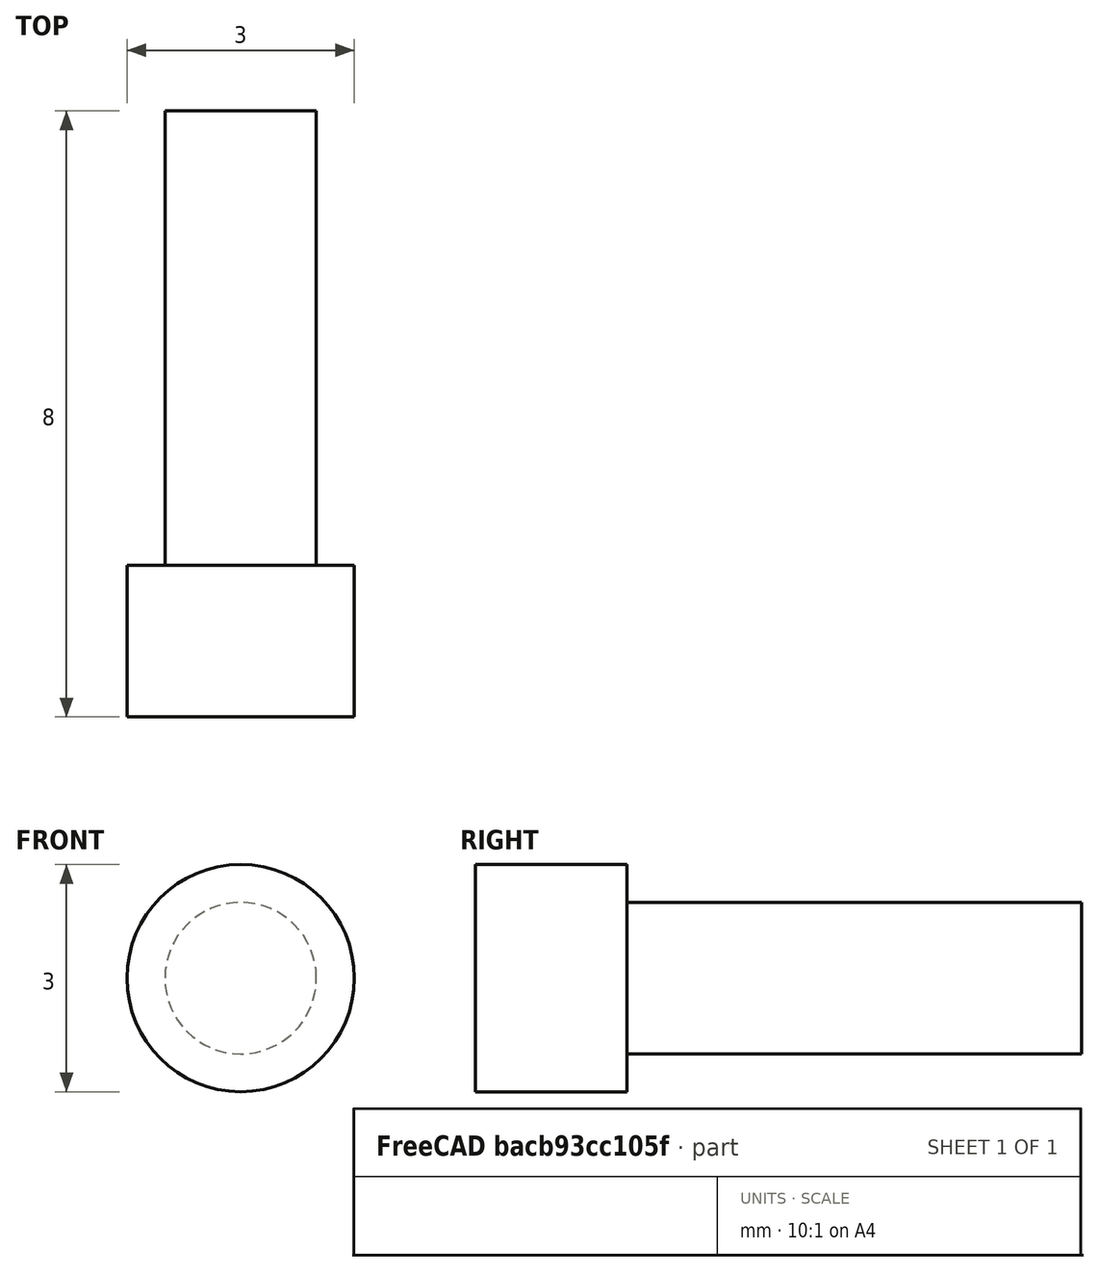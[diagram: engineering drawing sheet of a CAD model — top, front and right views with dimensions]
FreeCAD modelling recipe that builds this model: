
FCSTD DOCUMENT  (FreeCAD 1.0R39319 (Git))
Label: visM2L6
License: All rights reserved
LicenseURL: https://en.wikipedia.org/wiki/All_rights_reserved
objects: Sketcher::SketchObject×1, PartDesign::Revolution×1, PartDesign::Body×1
note: 6 computed .brp shape members not serialized (recipe doc carries the construction recipe); baked Part::Feature solids carry a one-line shape summary decoded from their .brp

FEATURE [Sketcher::SketchObject] Sketch
  ArcFitTolerance = 1e-06
  AttachmentSupport = -> [YZ_Plane]
  FullyConstrained = true
  MakeInternals = false
  MapMode = 5
  Placement = pos=(0,0,0) rot=(0.57735,0.57735,0.57735;2.0944rad)
  sketch-geometry (6):
    g0: LineSegment StartX=-2 StartY=0 StartZ=0 EndX=-2 EndY=1.5 EndZ=0
    g1: LineSegment StartX=-2 StartY=1.5 StartZ=0 EndX=-4.574e-13 EndY=1.5 EndZ=0
    g2: LineSegment StartX=-4.574e-13 StartY=1.5 StartZ=0 EndX=0 EndY=1 EndZ=0
    g3: LineSegment StartX=0 StartY=1 StartZ=0 EndX=6 EndY=1 EndZ=0
    g4: LineSegment StartX=6 StartY=0 StartZ=0 EndX=6 EndY=1 EndZ=0
    g5: LineSegment StartX=-2 StartY=0 StartZ=0 EndX=6 EndY=0 EndZ=0
  constraints (18):
    c: PointOnObject(g0,g-1)
    c: Vertical(g0)
    c: Coincident(g1,g0)
    c: PointOnObject(g1,g-2)
    c: Horizontal(g1)
    c: Coincident(g2,g1)
    c: PointOnObject(g2,g-2)
    c: Coincident(g3,g2)
    c: Horizontal(g3)
    c: PointOnObject(g4,g-1)
    c: Coincident(g5,g0)
    c: Coincident(g5,g4)
    c: Coincident(g4,g3)
    c: Perpendicular(g-1,g4)
    c: DistanceY(g0,g0) = 1.5
    c: DistanceX(g1,g1) = 2
    c: DistanceX(g3,g3) = 6
    c: DistanceY(g4,g4) = 1
FEATURE [PartDesign::Revolution] Revolution
  Angle = 360
  Angle2 = 60
  Axis = (1e-16,1,-1e-16)
  Base = (0,0,0)
  Placement = pos=(0,0,0) rot=(1,1,1;2.0944rad)
  Profile = -> Sketch
  ReferenceAxis = -> Y_Axis
  Refine = true
  Suppressed = false
  Type = 0
FEATURE [PartDesign::Body] Body  label="Corps"
  AllowCompound = false
  Group = -> [Sketch,Revolution]
  Origin = -> Origin
  Tip = -> Revolution
